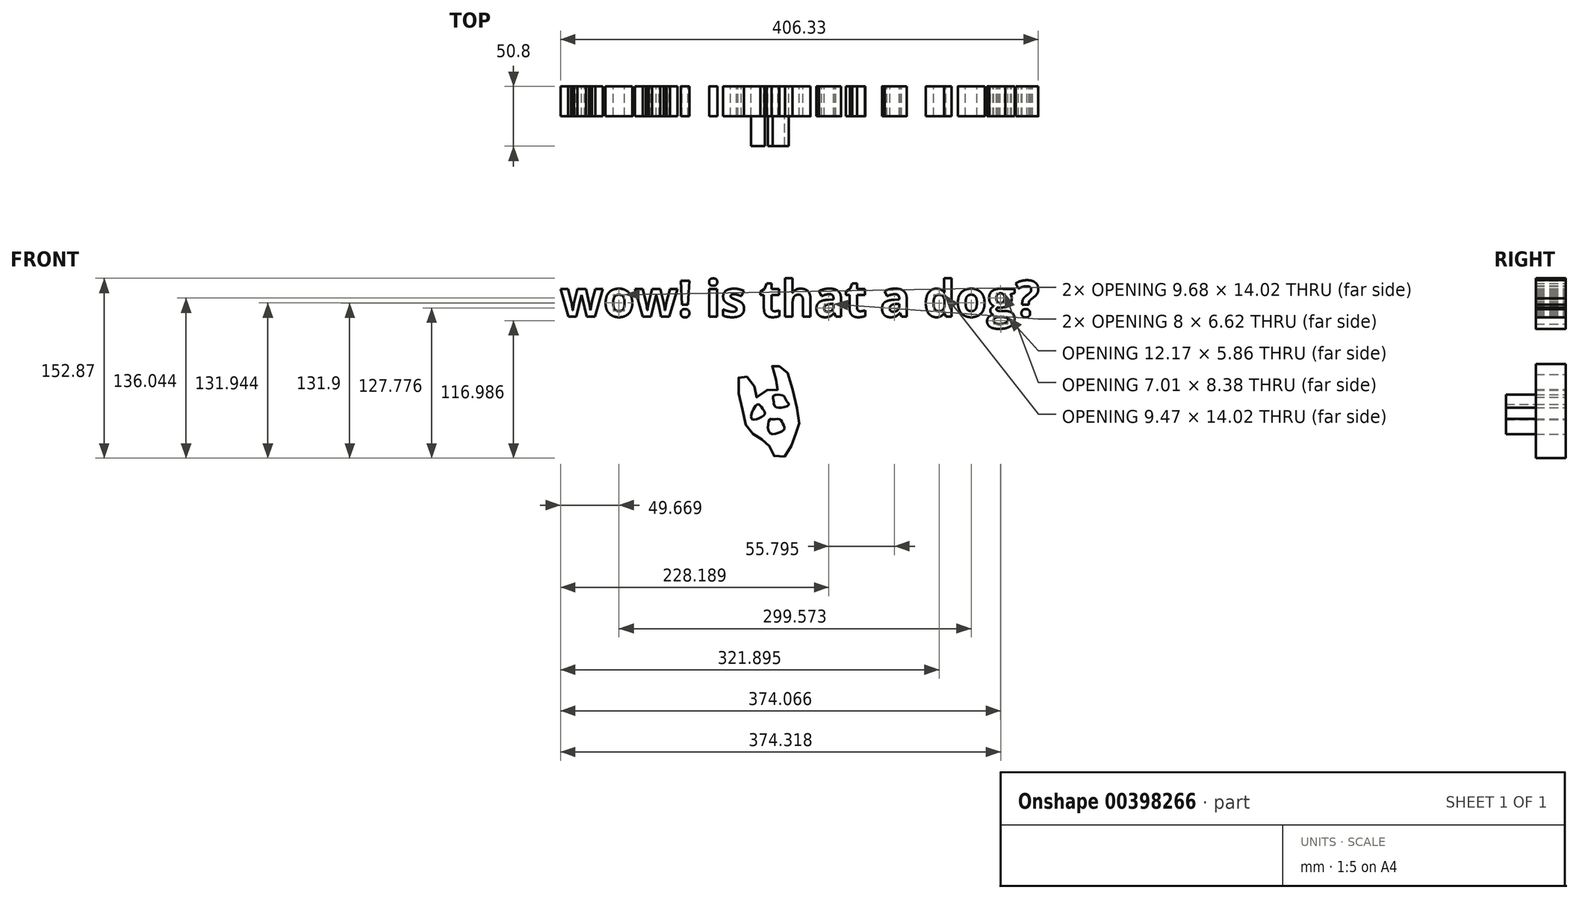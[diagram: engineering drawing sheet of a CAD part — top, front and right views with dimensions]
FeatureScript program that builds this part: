
annotation { "Feature Type Name" : "Feature", "Feature Type Description" : "" }
export const myFeature = defineFeature(function(context is Context, id is Id, definition is map)
    precondition{}
    {
        {
            var Q0;
            Q0=qCreatedBy(makeId("Front.planeOp"),FACE);
            var sketch = newSketch(context, id + "F0", { "sketchPlane" : qUnion([Q0])});
            skText(sketch, "E0", { "text": "wow! is that a dog?", "fontName": "OpenSans-Bold.ttf"});
            const initialGuessF0  = {"E0": [-0.2125, 0.01691, 1, 0, 0.03095]};
            skSetInitialGuess(sketch, initialGuessF0);
            skSolve(sketch);
        }
        {
            var Q0;
            Q0 = qSketchRegion(id + "F0", true);
            extrude(context, id + "F1", {"entities" : qUnion([Q0]), "depth" : 25.4 * mm});
        }
        {
            var Q0;
            Q0=qCreatedBy(makeId("Front.planeOp"),FACE);
            var sketch = newSketch(context, id + "F2", { "sketchPlane" : qUnion([Q0])});
            skFitSpline(sketch, "E1", {"points": [v(-57.2, -62.19) * mm, v(-61.17, -43.68) * mm, v(-58.94, -32.52) * mm, v(-51.92, -35.53) * mm, v(-46.7, -44.45) * mm, v(-45.12, -51.62) * mm, v(-36.16, -45.3) * mm, v(-28.12, -45.6) * mm, v(-27.32, -42.41) * mm, v(-30.8, -29.89) * mm, v(-31.5, -23.44) * mm, v(-24.68, -25.99) * mm, v(-19.1, -30.78) * mm, v(-13.57, -50.27) * mm, v(-9, -71.32) * mm, v(-10.43, -79.3) * mm, v(-14.66, -88.55) * mm, v(-18.72, -99.42) * mm, v(-27.13, -103.23) * mm, v(-32.7, -98.44) * mm, v(-35.45, -91.22) * mm, v(-41.28, -87.1) * mm, v(-47.59, -83.2) * mm, v(-53.81, -77) * mm, v(-57.2, -62.19) * mm]});
            skSolve(sketch);
        }
        {
            var Q0;
            Q0=qCreatedBy(makeId("Front.planeOp"),FACE);
            var sketch = newSketch(context, id + "F3", { "sketchPlane" : qUnion([Q0])});
            skFitSpline(sketch, "E2", {"points": [v(-48.98, -70.3) * mm, v(-48.24, -62.06) * mm, v(-43.48, -57.65) * mm, v(-39.73, -62.15) * mm, v(-38.49, -66.1) * mm, v(-48.98, -70.3) * mm]});
            skFitSpline(sketch, "E3", {"points": [v(-28.85, -60.03) * mm, v(-30.95, -54.2) * mm, v(-31.04, -50.3) * mm, v(-22.54, -50.4) * mm, v(-20.15, -54.38) * mm, v(-17.97, -57.9) * mm, v(-28.85, -60.03) * mm]});
            skFitSpline(sketch, "E4", {"points": [v(-33.98, -82.1) * mm, v(-34.13, -70.3) * mm, v(-31.72, -70.3) * mm, v(-25.72, -70.3) * mm, v(-22.26, -75.65) * mm, v(-21.92, -78.87) * mm, v(-33.98, -82.1) * mm]});
            skSolve(sketch);
        }
        {
            var Q0;
            Q0=makeQuery(id+"F3.imprint","IMPRINT",FACE,{"disambiguationData":[TD([[makeQuery(id+"F3.imprint","IMPRINT",EDGE,{"derivedFrom":sQuery(id+"F3.wireOp",EDGE,"E4")}),-1.0]])]});
            var Q1;
            Q1=makeQuery(id+"F3.imprint","IMPRINT",FACE,{"disambiguationData":[TD([[makeQuery(id+"F3.imprint","IMPRINT",EDGE,{"derivedFrom":sQuery(id+"F3.wireOp",EDGE,"E3")}),-1.0]])]});
            var Q2;
            Q2=makeQuery(id+"F3.imprint","IMPRINT",FACE,{"disambiguationData":[TD([[makeQuery(id+"F3.imprint","IMPRINT",EDGE,{"derivedFrom":sQuery(id+"F3.wireOp",EDGE,"E2")}),-1.0]])]});
            extrude(context, id + "F4", {"entities" : qUnion([Q0, Q1, Q2]), "depth" : 25.4 * mm});
        }
        {
            var Q0;
            Q0=makeQuery(id+"F2.imprint","IMPRINT",FACE,{"disambiguationData":[TD([[makeQuery(id+"F2.imprint","IMPRINT",EDGE,{"derivedFrom":sQuery(id+"F2.wireOp",EDGE,"E1")}),-1.0]])]});
            var Q1;
            Q1=makeQuery(id+"F4.opExtrude","CAP_FACE",FACE,{"disambiguationData":[OSD([sQuery(id+"F3.wireOp",EDGE,"E2")])],"isStart":false});
            var Q2;
            Q2=makeQuery(id+"F4.opExtrude","CAP_FACE",FACE,{"disambiguationData":[OSD([sQuery(id+"F3.wireOp",EDGE,"E2")])],"isStart":true});
            var Q3;
            Q3=makeQuery(id+"F4.opExtrude","CAP_FACE",FACE,{"disambiguationData":[OSD([sQuery(id+"F3.wireOp",EDGE,"E3")])],"isStart":false});
            var Q4;
            Q4=makeQuery(id+"F4.opExtrude","CAP_FACE",FACE,{"disambiguationData":[OSD([sQuery(id+"F3.wireOp",EDGE,"E4")])],"isStart":false});
            var Q5;
            Q5=makeQuery(id+"F4.opExtrude","CAP_FACE",FACE,{"disambiguationData":[OSD([sQuery(id+"F3.wireOp",EDGE,"E4")])],"isStart":true});
            var Q6;
            Q6=makeQuery(id+"F4.opExtrude","CAP_FACE",FACE,{"disambiguationData":[OSD([sQuery(id+"F3.wireOp",EDGE,"E3")])],"isStart":true});
            extrude(context, id + "F5", {"entities" : qUnion([Q0, Q1, Q2, Q3, Q4, Q5, Q6]), "depth" : 25.4 * mm});
        }
    });
